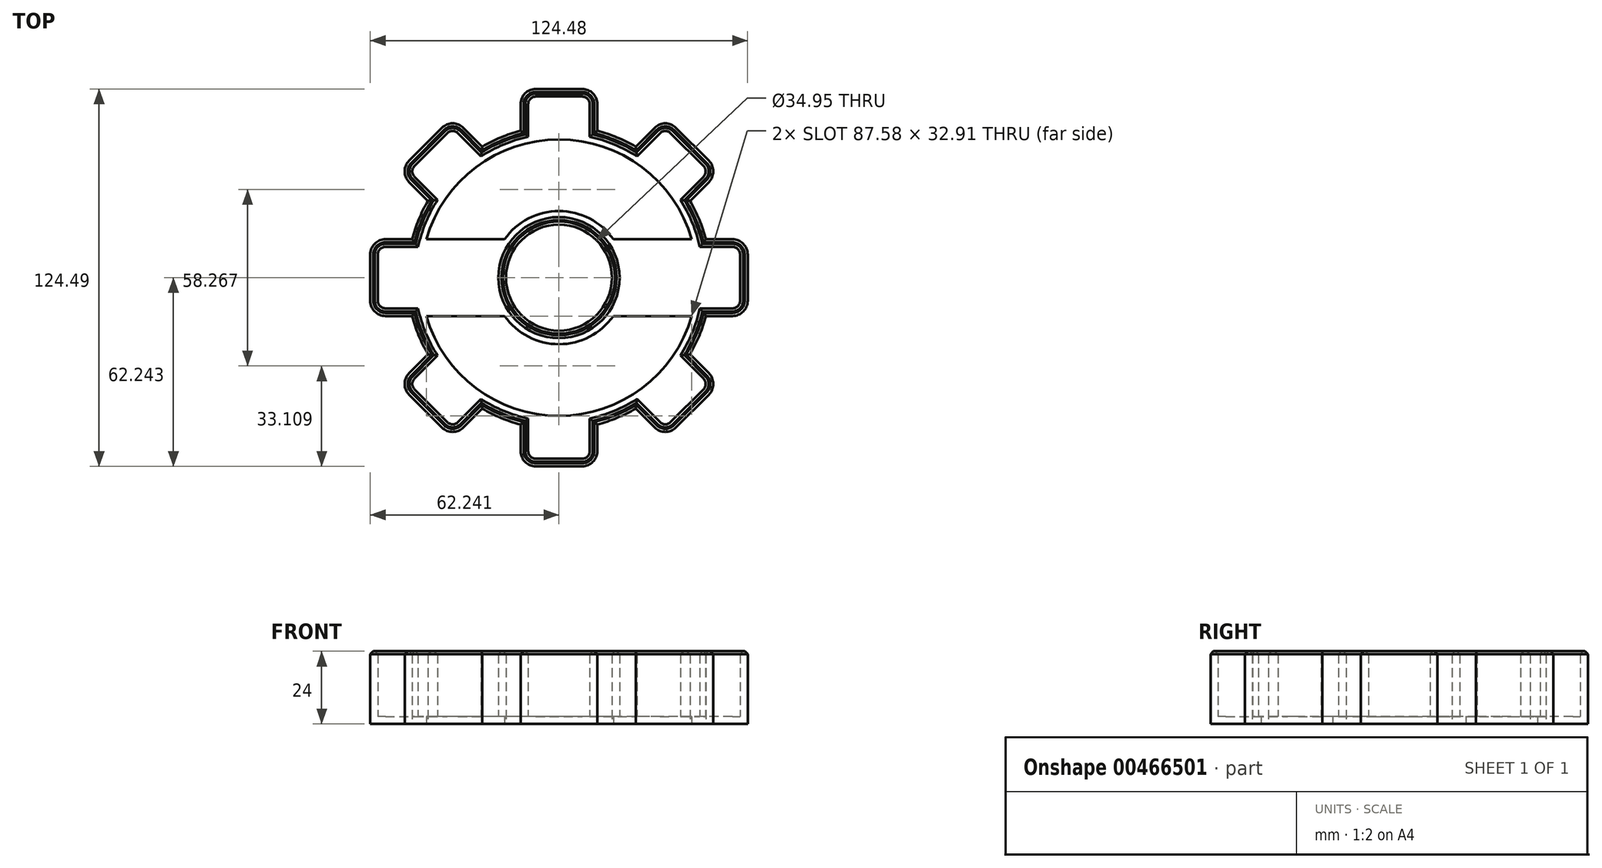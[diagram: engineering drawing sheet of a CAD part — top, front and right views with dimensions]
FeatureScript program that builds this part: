
annotation { "Feature Type Name" : "Feature", "Feature Type Description" : "" }
export const myFeature = defineFeature(function(context is Context, id is Id, definition is map)
    precondition{}
    {
        {
            var Q0;
            Q0=qCreatedBy(makeId("Top.planeOp"),FACE);
            var sketch = newSketch(context, id + "F0", { "sketchPlane" : qUnion([Q0])});
            skCircle(sketch, "E0", {"center": v(-6.85, -8.47) * mm, "radius": 17.48 * mm});
            skCircle(sketch, "E1", {"center": v(-6.85, -8.47) * mm, "radius": 50.07 * mm});
            skSolve(sketch);
        }
        {
            var Q0;
            Q0=qCreatedBy(makeId("Top.planeOp"),FACE);
            var sketch = newSketch(context, id + "F1", { "sketchPlane" : qUnion([Q0])});
            skLineSegment(sketch, "E2.bottom", {"start": v(-14.5, 53.78) * mm, "end": v(0.8, 53.78) * mm});
            skLineSegment(sketch, "E2.top", {"start": v(-19.5, 39.98) * mm, "end": v(5.8, 39.98) * mm});
            skLineSegment(sketch, "E2.left", {"start": v(-19.5, 48.78) * mm, "end": v(-19.5, 39.98) * mm});
            skLineSegment(sketch, "E2.right", {"start": v(5.8, 48.78) * mm, "end": v(5.8, 39.98) * mm});
            skPoint(sketch, "E3.visualSharp", {"position": v(-19.5, 53.78) * mm});
            skArc(sketch, "E3.filletArc", {"start": v(-14.5, 53.78) * mm, "mid": v(-18.03, 52.31) * mm, "end": v(-19.5, 48.78) * mm});
            skPoint(sketch, "E4.visualSharp", {"position": v(5.8, 53.78) * mm});
            skArc(sketch, "E4.filletArc", {"start": v(5.8, 48.78) * mm, "mid": v(4.33, 52.31) * mm, "end": v(0.8, 53.78) * mm});
            skSolve(sketch);
        }
        {
            var Q0;
            Q0=makeQuery(id+"F0.imprint","IMPRINT",FACE,{"disambiguationData":[TD([[makeQuery(id+"F0.imprint","IMPRINT",EDGE,{"derivedFrom":sQuery(id+"F0.wireOp",EDGE,"E0")}),-1.0]])]});
            var Q1;
            Q1 = qSketchRegion(id + "F1", true);
            extrude(context, id + "F2", {"entities" : qUnion([Q0, Q1]), "depth" : 24 * mm});
        }
        {
            var Q0;
            Q0=makeQuery(id+"F2.opExtrude","SWEPT_BODY",BODY,{"disambiguationData":[OSD([sQuery(id+"F1.wireOp",EDGE,"E2.bottom"),sQuery(id+"F1.wireOp",EDGE,"E2.top"),sQuery(id+"F1.wireOp",EDGE,"E2.left"),sQuery(id+"F1.wireOp",EDGE,"E2.right"),sQuery(id+"F1.wireOp",EDGE,"E3.filletArc"),sQuery(id+"F1.wireOp",EDGE,"E4.filletArc")])]});
            var Q1;
            Q1=sQuery(id+"F0.wireOp",EDGE,"E0");
            circularPattern(context, id + "F3", {"entities" : qUnion([Q0]), "axis" : qUnion([Q1]), "angle" : 360 * degree, "instanceCount" : 8, "equalSpace" : true});
        }
        {
            var Q0;
            Q0=makeQuery(id+"F2.opExtrude","SWEPT_BODY",BODY,{"disambiguationData":[OSD([sQuery(id+"F1.wireOp",EDGE,"E2.bottom"),sQuery(id+"F1.wireOp",EDGE,"E2.top"),sQuery(id+"F1.wireOp",EDGE,"E2.left"),sQuery(id+"F1.wireOp",EDGE,"E2.right"),sQuery(id+"F1.wireOp",EDGE,"E3.filletArc"),sQuery(id+"F1.wireOp",EDGE,"E4.filletArc")])]});
            var Q1;
            Q1=makeQuery(id+"F3.opPattern","COPY",BODY,{"derivedFrom":makeQuery(id+"F2.opExtrude","SWEPT_BODY",BODY,{"disambiguationData":[OSD([sQuery(id+"F1.wireOp",EDGE,"E2.bottom"),sQuery(id+"F1.wireOp",EDGE,"E2.top"),sQuery(id+"F1.wireOp",EDGE,"E2.left"),sQuery(id+"F1.wireOp",EDGE,"E2.right"),sQuery(id+"F1.wireOp",EDGE,"E3.filletArc"),sQuery(id+"F1.wireOp",EDGE,"E4.filletArc")])]}),"instanceName":"7"});
            var Q2;
            Q2=makeQuery(id+"F3.opPattern","COPY",BODY,{"derivedFrom":makeQuery(id+"F2.opExtrude","SWEPT_BODY",BODY,{"disambiguationData":[OSD([sQuery(id+"F1.wireOp",EDGE,"E2.bottom"),sQuery(id+"F1.wireOp",EDGE,"E2.top"),sQuery(id+"F1.wireOp",EDGE,"E2.left"),sQuery(id+"F1.wireOp",EDGE,"E2.right"),sQuery(id+"F1.wireOp",EDGE,"E3.filletArc"),sQuery(id+"F1.wireOp",EDGE,"E4.filletArc")])]}),"instanceName":"6"});
            var Q3;
            Q3=makeQuery(id+"F3.opPattern","COPY",BODY,{"derivedFrom":makeQuery(id+"F2.opExtrude","SWEPT_BODY",BODY,{"disambiguationData":[OSD([sQuery(id+"F1.wireOp",EDGE,"E2.bottom"),sQuery(id+"F1.wireOp",EDGE,"E2.top"),sQuery(id+"F1.wireOp",EDGE,"E2.left"),sQuery(id+"F1.wireOp",EDGE,"E2.right"),sQuery(id+"F1.wireOp",EDGE,"E3.filletArc"),sQuery(id+"F1.wireOp",EDGE,"E4.filletArc")])]}),"instanceName":"5"});
            var Q4;
            Q4=makeQuery(id+"F3.opPattern","COPY",BODY,{"derivedFrom":makeQuery(id+"F2.opExtrude","SWEPT_BODY",BODY,{"disambiguationData":[OSD([sQuery(id+"F1.wireOp",EDGE,"E2.bottom"),sQuery(id+"F1.wireOp",EDGE,"E2.top"),sQuery(id+"F1.wireOp",EDGE,"E2.left"),sQuery(id+"F1.wireOp",EDGE,"E2.right"),sQuery(id+"F1.wireOp",EDGE,"E3.filletArc"),sQuery(id+"F1.wireOp",EDGE,"E4.filletArc")])]}),"instanceName":"4"});
            var Q5;
            Q5=makeQuery(id+"F3.opPattern","COPY",BODY,{"derivedFrom":makeQuery(id+"F2.opExtrude","SWEPT_BODY",BODY,{"disambiguationData":[OSD([sQuery(id+"F1.wireOp",EDGE,"E2.bottom"),sQuery(id+"F1.wireOp",EDGE,"E2.top"),sQuery(id+"F1.wireOp",EDGE,"E2.left"),sQuery(id+"F1.wireOp",EDGE,"E2.right"),sQuery(id+"F1.wireOp",EDGE,"E3.filletArc"),sQuery(id+"F1.wireOp",EDGE,"E4.filletArc")])]}),"instanceName":"3"});
            var Q6;
            Q6=makeQuery(id+"F3.opPattern","COPY",BODY,{"derivedFrom":makeQuery(id+"F2.opExtrude","SWEPT_BODY",BODY,{"disambiguationData":[OSD([sQuery(id+"F1.wireOp",EDGE,"E2.bottom"),sQuery(id+"F1.wireOp",EDGE,"E2.top"),sQuery(id+"F1.wireOp",EDGE,"E2.left"),sQuery(id+"F1.wireOp",EDGE,"E2.right"),sQuery(id+"F1.wireOp",EDGE,"E3.filletArc"),sQuery(id+"F1.wireOp",EDGE,"E4.filletArc")])]}),"instanceName":"2"});
            var Q7;
            Q7=makeQuery(id+"F3.opPattern","COPY",BODY,{"derivedFrom":makeQuery(id+"F2.opExtrude","SWEPT_BODY",BODY,{"disambiguationData":[OSD([sQuery(id+"F1.wireOp",EDGE,"E2.bottom"),sQuery(id+"F1.wireOp",EDGE,"E2.top"),sQuery(id+"F1.wireOp",EDGE,"E2.left"),sQuery(id+"F1.wireOp",EDGE,"E2.right"),sQuery(id+"F1.wireOp",EDGE,"E3.filletArc"),sQuery(id+"F1.wireOp",EDGE,"E4.filletArc")])]}),"instanceName":"1"});
            var Q8;
            Q8=makeQuery(id+"F2.opExtrude","SWEPT_BODY",BODY,{"disambiguationData":[OSD([sQuery(id+"F0.wireOp",EDGE,"E0"),sQuery(id+"F0.wireOp",EDGE,"E1")])]});
            booleanBodies(context, id + "F4", {"operationType" : BooleanOperationType.UNION, "tools" : qUnion([Q0, Q1, Q2, Q3, Q4, Q5, Q6, Q7, Q8])});
        }
        {
            var Q0;
            {var subQ0=makeQuery(id+"F2.opExtrude","CAP_FACE",FACE,{"disambiguationData":[OSD([sQuery(id+"F1.wireOp",EDGE,"E2.bottom"),sQuery(id+"F1.wireOp",EDGE,"E2.top"),sQuery(id+"F1.wireOp",EDGE,"E2.left"),sQuery(id+"F1.wireOp",EDGE,"E2.right"),sQuery(id+"F1.wireOp",EDGE,"E3.filletArc"),sQuery(id+"F1.wireOp",EDGE,"E4.filletArc")])],"isStart":false});Q0=makeQuery(id+"F4.opBoolean","MERGE",FACE,{"derivedFrom":[makeQuery(id+"F2.opExtrude","CAP_FACE",FACE,{"disambiguationData":[OSD([sQuery(id+"F0.wireOp",EDGE,"E0"),sQuery(id+"F0.wireOp",EDGE,"E1")])],"isStart":false}),subQ0,makeQuery(id+"F3.opPattern","COPY",FACE,{"derivedFrom":subQ0,"instanceName":"1"}),makeQuery(id+"F3.opPattern","COPY",FACE,{"derivedFrom":subQ0,"instanceName":"2"}),makeQuery(id+"F3.opPattern","COPY",FACE,{"derivedFrom":subQ0,"instanceName":"3"}),makeQuery(id+"F3.opPattern","COPY",FACE,{"derivedFrom":subQ0,"instanceName":"4"}),makeQuery(id+"F3.opPattern","COPY",FACE,{"derivedFrom":subQ0,"instanceName":"5"}),makeQuery(id+"F3.opPattern","COPY",FACE,{"derivedFrom":subQ0,"instanceName":"6"}),makeQuery(id+"F3.opPattern","COPY",FACE,{"derivedFrom":subQ0,"instanceName":"7"})]});}
            shell(context, id + "F5", {"entities" : qUnion([Q0]), "thickness" : 2.5 * mm});
        }
        {
            var Q0;
            {var subQ0=sQuery(id+"F1.wireOp",EDGE,"E4.filletArc");var subQ1=sQuery(id+"F1.wireOp",EDGE,"E3.filletArc");var subQ2=sQuery(id+"F1.wireOp",EDGE,"E2.right");var subQ3=sQuery(id+"F1.wireOp",EDGE,"E2.left");var subQ4=sQuery(id+"F1.wireOp",EDGE,"E2.top");var subQ5=sQuery(id+"F1.wireOp",EDGE,"E2.bottom");var subQ6=makeQuery(id+"F2.opExtrude","CAP_FACE",FACE,{"disambiguationData":[OSD([subQ5,subQ4,subQ3,subQ2,subQ1,subQ0])],"isStart":false});var subQ7=sQuery(id+"F0.wireOp",EDGE,"E1");var subQ8=sQuery(id+"F0.wireOp",EDGE,"E0");Q0=makeQuery(id+"F5.opShell","OFFSET_FACE",FACE,{"disambiguationData":[OSD([subQ8,subQ7,subQ5,subQ4,subQ3,subQ2,subQ1,subQ0]),TDD([makeQuery(id+"F4.opBoolean","MERGE",FACE,{"derivedFrom":[makeQuery(id+"F2.opExtrude","CAP_FACE",FACE,{"disambiguationData":[OSD([subQ8,subQ7])],"isStart":false}),subQ6,makeQuery(id+"F3.opPattern","COPY",FACE,{"derivedFrom":subQ6,"instanceName":"1"}),makeQuery(id+"F3.opPattern","COPY",FACE,{"derivedFrom":subQ6,"instanceName":"2"}),makeQuery(id+"F3.opPattern","COPY",FACE,{"derivedFrom":subQ6,"instanceName":"3"}),makeQuery(id+"F3.opPattern","COPY",FACE,{"derivedFrom":subQ6,"instanceName":"4"}),makeQuery(id+"F3.opPattern","COPY",FACE,{"derivedFrom":subQ6,"instanceName":"5"}),makeQuery(id+"F3.opPattern","COPY",FACE,{"derivedFrom":subQ6,"instanceName":"6"}),makeQuery(id+"F3.opPattern","COPY",FACE,{"derivedFrom":subQ6,"instanceName":"7"})]})])]});}
            var Q1;
            {var subQ0=makeQuery(id+"F2.opExtrude","CAP_FACE",FACE,{"disambiguationData":[OSD([sQuery(id+"F1.wireOp",EDGE,"E2.bottom"),sQuery(id+"F1.wireOp",EDGE,"E2.top"),sQuery(id+"F1.wireOp",EDGE,"E2.left"),sQuery(id+"F1.wireOp",EDGE,"E2.right"),sQuery(id+"F1.wireOp",EDGE,"E3.filletArc"),sQuery(id+"F1.wireOp",EDGE,"E4.filletArc")])],"isStart":false});Q1=makeQuery(id+"F4.opBoolean","MERGE",FACE,{"derivedFrom":[makeQuery(id+"F2.opExtrude","CAP_FACE",FACE,{"disambiguationData":[OSD([sQuery(id+"F0.wireOp",EDGE,"E0"),sQuery(id+"F0.wireOp",EDGE,"E1")])],"isStart":false}),subQ0,makeQuery(id+"F3.opPattern","COPY",FACE,{"derivedFrom":subQ0,"instanceName":"1"}),makeQuery(id+"F3.opPattern","COPY",FACE,{"derivedFrom":subQ0,"instanceName":"2"}),makeQuery(id+"F3.opPattern","COPY",FACE,{"derivedFrom":subQ0,"instanceName":"3"}),makeQuery(id+"F3.opPattern","COPY",FACE,{"derivedFrom":subQ0,"instanceName":"4"}),makeQuery(id+"F3.opPattern","COPY",FACE,{"derivedFrom":subQ0,"instanceName":"5"}),makeQuery(id+"F3.opPattern","COPY",FACE,{"derivedFrom":subQ0,"instanceName":"6"}),makeQuery(id+"F3.opPattern","COPY",FACE,{"derivedFrom":subQ0,"instanceName":"7"})]});}
            chamfer(context, id + "F6", {"entities" : qUnion([Q0, Q1]), "width" : 1 * mm, "tangentPropagation" : true});
        }
        {
            var Q0;
            Q0=makeQuery(id+"F0.imprint","IMPRINT",FACE,{"disambiguationData":[TD([[makeQuery(id+"F0.imprint","IMPRINT",EDGE,{"derivedFrom":sQuery(id+"F0.wireOp",EDGE,"E0")}),-1.0]])]});
            var sketch = newSketch(context, id + "F7", { "sketchPlane" : qUnion([Q0])});
            skArc(sketch, "E5", {"start": v(-50.64, -21.15) * mm, "mid": v(-6.85, -54.06) * mm, "end": v(36.94, -21.15) * mm});
            skArc(sketch, "E6", {"start": v(-24.78, -21.15) * mm, "mid": v(-6.85, -30.42) * mm, "end": v(11.08, -21.15) * mm});
            skLineSegment(sketch, "E7.bottom", {"start": v(-50.64, -21.15) * mm, "end": v(-24.78, -21.15) * mm});
            skLineSegment(sketch, "E7.top", {"start": v(-50.64, 4.21) * mm, "end": v(-24.78, 4.21) * mm});
            skLineSegment(sketch, "E8.trimOffspring", {"start": v(11.08, -21.15) * mm, "end": v(36.94, -21.15) * mm});
            skLineSegment(sketch, "E9.trimOffspring", {"start": v(11.08, 4.21) * mm, "end": v(36.94, 4.21) * mm});
            skArc(sketch, "E10.trimOffspring", {"start": v(36.94, 4.21) * mm, "mid": v(-6.85, 37.12) * mm, "end": v(-50.64, 4.21) * mm});
            skArc(sketch, "E11.trimOffspring", {"start": v(11.08, 4.21) * mm, "mid": v(-6.85, 13.49) * mm, "end": v(-24.78, 4.21) * mm});
            skSolve(sketch);
        }
        {
            var Q0;
            Q0=makeQuery(id+"F7.imprint","IMPRINT",FACE,{"disambiguationData":[TD([[makeQuery(id+"F7.imprint","IMPRINT",EDGE,{"derivedFrom":sQuery(id+"F7.wireOp",EDGE,"E5")}),1.0]])]});
            var Q1;
            Q1=makeQuery(id+"F7.imprint","IMPRINT",FACE,{"disambiguationData":[TD([[makeQuery(id+"F7.imprint","IMPRINT",EDGE,{"derivedFrom":sQuery(id+"F7.wireOp",EDGE,"E7.top")}),1.0]])]});
            extrude(context, id + "F8", {"entities" : qUnion([Q0, Q1]), "operationType" : NewBodyOperationType.REMOVE, "depth" : 5 * mm});
        }
    });
